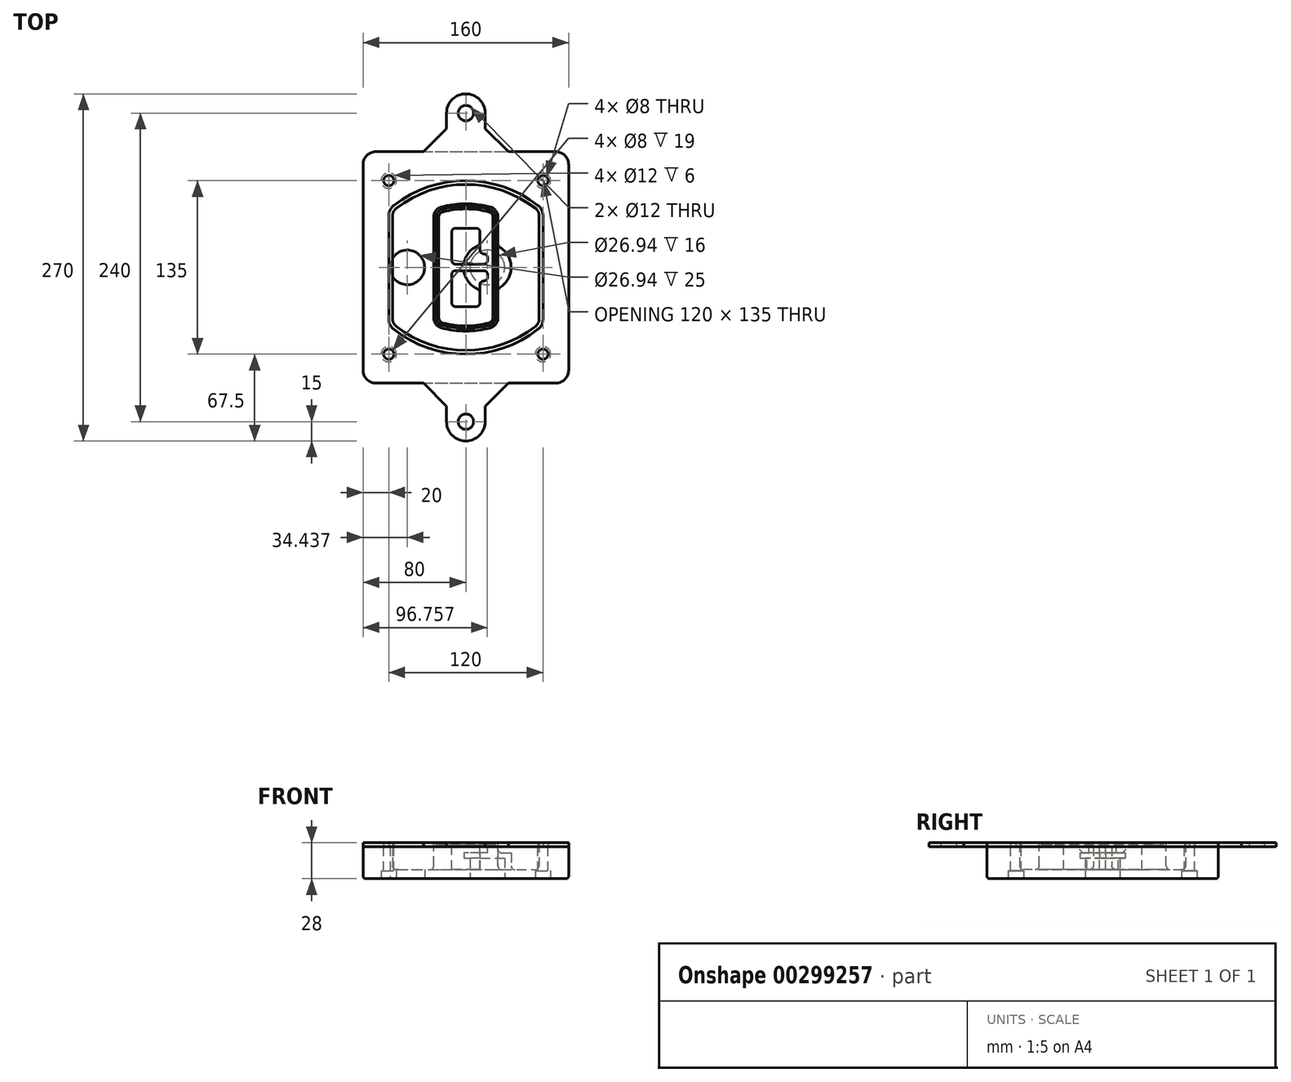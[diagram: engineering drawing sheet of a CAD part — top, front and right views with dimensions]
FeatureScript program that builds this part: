
annotation { "Feature Type Name" : "Feature", "Feature Type Description" : "" }
export const myFeature = defineFeature(function(context is Context, id is Id, definition is map)
    precondition{}
    {
        {
            var Q0;
            Q0=qCreatedBy(makeId("Top.planeOp"),FACE);
            var sketch = newSketch(context, id + "F0", { "sketchPlane" : qUnion([Q0])});
            skPoint(sketch, "E0.rect.middle", {"position": v(0, 0) * mm});
            skLineSegment(sketch, "E1.bottom", {"start": v(-70, -90) * mm, "end": v(70, -90) * mm});
            skLineSegment(sketch, "E1.top", {"start": v(-70, 90) * mm, "end": v(70, 90) * mm});
            skLineSegment(sketch, "E1.left", {"start": v(-80, -80) * mm, "end": v(-80, 80) * mm});
            skLineSegment(sketch, "E1.right", {"start": v(80, -80) * mm, "end": v(80, 80) * mm});
            skLineSegment(sketch, "E2", {"start": v(-80, 90) * mm, "end": v(80, -90) * mm, "construction": true});
            skLineSegment(sketch, "E3", {"start": v(80, 90) * mm, "end": v(-80, -90) * mm, "construction": true});
            skCircle(sketch, "E4", {"center": v(-60, 67.5) * mm, "radius": 4 * mm});
            skCircle(sketch, "E5", {"center": v(60, 67.5) * mm, "radius": 4 * mm});
            skCircle(sketch, "E6", {"center": v(60, -67.5) * mm, "radius": 4 * mm});
            skCircle(sketch, "E7", {"center": v(-60, -67.5) * mm, "radius": 4 * mm});
            skLineSegment(sketch, "E8", {"start": v(-60, 67.5) * mm, "end": v(60, 67.5) * mm, "construction": true});
            skLineSegment(sketch, "E9", {"start": v(60, 67.5) * mm, "end": v(60, -67.5) * mm, "construction": true});
            skLineSegment(sketch, "E10", {"start": v(60, -67.5) * mm, "end": v(-60, -67.5) * mm, "construction": true});
            skLineSegment(sketch, "E11", {"start": v(-60, -67.5) * mm, "end": v(-60, 67.5) * mm, "construction": true});
            skLineSegment(sketch, "E12", {"start": v(-60, 40.3) * mm, "end": v(-60, -40.3) * mm});
            skLineSegment(sketch, "E13", {"start": v(60, 40.3) * mm, "end": v(60, -40.3) * mm});
            skArc(sketch, "E14", {"start": v(56.15, 48.18) * mm, "mid": v(0, 67.5) * mm, "end": v(-56.15, 48.18) * mm});
            skArc(sketch, "E15", {"start": v(-56.15, -48.18) * mm, "mid": v(0, -67.5) * mm, "end": v(56.15, -48.18) * mm});
            skLineSegment(sketch, "E16", {"start": v(-60, 0) * mm, "end": v(60, 0) * mm, "construction": true});
            skPoint(sketch, "E17.visualSharp", {"position": v(-60, -45) * mm});
            skArc(sketch, "E17.filletArc", {"start": v(-60, -40.3) * mm, "mid": v(-58.99, -44.68) * mm, "end": v(-56.15, -48.18) * mm});
            skPoint(sketch, "E18.visualSharp", {"position": v(-60, 45) * mm});
            skArc(sketch, "E18.filletArc", {"start": v(-56.15, 48.18) * mm, "mid": v(-58.99, 44.68) * mm, "end": v(-60, 40.3) * mm});
            skPoint(sketch, "E19.visualSharp", {"position": v(60, 45) * mm});
            skArc(sketch, "E19.filletArc", {"start": v(60, 40.3) * mm, "mid": v(58.99, 44.68) * mm, "end": v(56.15, 48.18) * mm});
            skPoint(sketch, "E20.visualSharp", {"position": v(60, -45) * mm});
            skArc(sketch, "E20.filletArc", {"start": v(56.15, -48.18) * mm, "mid": v(58.99, -44.68) * mm, "end": v(60, -40.3) * mm});
            skPoint(sketch, "E21.visualSharp", {"position": v(-80, 90) * mm});
            skArc(sketch, "E21.filletArc", {"start": v(-70, 90) * mm, "mid": v(-77.07, 87.07) * mm, "end": v(-80, 80) * mm});
            skPoint(sketch, "E22.visualSharp", {"position": v(80, 90) * mm});
            skArc(sketch, "E22.filletArc", {"start": v(80, 80) * mm, "mid": v(77.07, 87.07) * mm, "end": v(70, 90) * mm});
            skPoint(sketch, "E23.visualSharp", {"position": v(80, -90) * mm});
            skArc(sketch, "E23.filletArc", {"start": v(70, -90) * mm, "mid": v(77.07, -87.07) * mm, "end": v(80, -80) * mm});
            skPoint(sketch, "E24.visualSharp", {"position": v(-80, -90) * mm});
            skArc(sketch, "E24.filletArc", {"start": v(-80, -80) * mm, "mid": v(-77.07, -87.07) * mm, "end": v(-70, -90) * mm});
            skArc(sketch, "E25.0", {"start": v(57, 40.3) * mm, "mid": v(56.3, 43.36) * mm, "end": v(54.3, 45.81) * mm});
            skLineSegment(sketch, "E25.1", {"start": v(57, 40.3) * mm, "end": v(57, -40.3) * mm});
            skArc(sketch, "E25.2", {"start": v(54.3, -45.81) * mm, "mid": v(56.3, -43.36) * mm, "end": v(57, -40.3) * mm});
            skArc(sketch, "E25.3", {"start": v(-54.3, -45.81) * mm, "mid": v(0, -64.5) * mm, "end": v(54.3, -45.81) * mm});
            skArc(sketch, "E25.4", {"start": v(-57, -40.3) * mm, "mid": v(-56.3, -43.36) * mm, "end": v(-54.3, -45.81) * mm});
            skArc(sketch, "E25.5", {"start": v(54.3, 45.81) * mm, "mid": v(0, 64.5) * mm, "end": v(-54.3, 45.81) * mm});
            skLineSegment(sketch, "E25.6", {"start": v(-57, 40.3) * mm, "end": v(-57, -40.3) * mm});
            skArc(sketch, "E25.7", {"start": v(-54.3, 45.81) * mm, "mid": v(-56.3, 43.36) * mm, "end": v(-57, 40.3) * mm});
            skArc(sketch, "E26.0", {"start": v(-58.62, 51.33) * mm, "mid": v(-62.58, 46.43) * mm, "end": v(-64, 40.3) * mm});
            skArc(sketch, "E26.1", {"start": v(58.62, 51.33) * mm, "mid": v(0, 71.5) * mm, "end": v(-58.62, 51.33) * mm});
            skArc(sketch, "E26.2", {"start": v(64, 40.3) * mm, "mid": v(62.58, 46.43) * mm, "end": v(58.62, 51.33) * mm});
            skLineSegment(sketch, "E26.3", {"start": v(64, 40.3) * mm, "end": v(64, -40.3) * mm});
            skArc(sketch, "E26.4", {"start": v(58.62, -51.33) * mm, "mid": v(62.58, -46.43) * mm, "end": v(64, -40.3) * mm});
            skLineSegment(sketch, "E26.5", {"start": v(-64, 40.3) * mm, "end": v(-64, -40.3) * mm});
            skArc(sketch, "E26.6", {"start": v(-58.62, -51.33) * mm, "mid": v(0, -71.5) * mm, "end": v(58.62, -51.33) * mm});
            skArc(sketch, "E26.7", {"start": v(-64, -40.3) * mm, "mid": v(-62.58, -46.43) * mm, "end": v(-58.62, -51.33) * mm});
            skSolve(sketch);
        }
        {
            var Q0;
            Q0=makeQuery(id+"F0.imprint","IMPRINT",FACE,{"disambiguationData":[TD([[makeQuery(id+"F0.imprint","IMPRINT",EDGE,{"derivedFrom":sQuery(id+"F0.wireOp",EDGE,"E1.bottom")}),1.0]])]});
            var Q1;
            Q1=makeQuery(id+"F0.imprint","IMPRINT",FACE,{"disambiguationData":[TD([[makeQuery(id+"F0.imprint","IMPRINT",EDGE,{"derivedFrom":sQuery(id+"F0.wireOp",EDGE,"E12")}),1.0]])]});
            var Q2;
            Q2=makeQuery(id+"F0.imprint","IMPRINT",FACE,{"disambiguationData":[TD([[makeQuery(id+"F0.imprint","IMPRINT",EDGE,{"derivedFrom":sQuery(id+"F0.wireOp",EDGE,"E25.0")}),1.0]])]});
            var Q3;
            Q3=makeQuery(id+"F0.imprint","IMPRINT",FACE,{"disambiguationData":[TD([[makeQuery(id+"F0.imprint","IMPRINT",EDGE,{"derivedFrom":sQuery(id+"F0.wireOp",EDGE,"E12")}),-1.0]])]});
            extrude(context, id + "F1", {"entities" : qUnion([Q0, Q1, Q2, Q3]), "oppositeDirection" : true, "depth" : 25 * mm});
        }
        {
            var Q0;
            Q0=makeQuery(id+"F0.imprint","IMPRINT",FACE,{"disambiguationData":[TD([[makeQuery(id+"F0.imprint","IMPRINT",EDGE,{"derivedFrom":sQuery(id+"F0.wireOp",EDGE,"E12")}),1.0]])]});
            extrude(context, id + "F2", {"entities" : qUnion([Q0]), "operationType" : NewBodyOperationType.ADD, "depth" : 3 * mm});
        }
        {
            var Q0;
            Q0=makeQuery(id+"F0.imprint","IMPRINT",FACE,{"disambiguationData":[TD([[makeQuery(id+"F0.imprint","IMPRINT",EDGE,{"derivedFrom":sQuery(id+"F0.wireOp",EDGE,"E25.0")}),1.0]])]});
            extrude(context, id + "F3", {"entities" : qUnion([Q0]), "operationType" : NewBodyOperationType.REMOVE, "oppositeDirection" : true, "depth" : 18 * mm});
        }
        {
            var Q0;
            Q0=makeQuery(id+"F2.opExtrude","CAP_FACE",FACE,{"disambiguationData":[OSD([sQuery(id+"F0.wireOp",EDGE,"E12"),sQuery(id+"F0.wireOp",EDGE,"E13"),sQuery(id+"F0.wireOp",EDGE,"E14"),sQuery(id+"F0.wireOp",EDGE,"E15"),sQuery(id+"F0.wireOp",EDGE,"E17.filletArc"),sQuery(id+"F0.wireOp",EDGE,"E18.filletArc"),sQuery(id+"F0.wireOp",EDGE,"E19.filletArc"),sQuery(id+"F0.wireOp",EDGE,"E20.filletArc"),sQuery(id+"F0.wireOp",EDGE,"E25.0"),sQuery(id+"F0.wireOp",EDGE,"E25.1"),sQuery(id+"F0.wireOp",EDGE,"E25.2"),sQuery(id+"F0.wireOp",EDGE,"E25.3"),sQuery(id+"F0.wireOp",EDGE,"E25.4"),sQuery(id+"F0.wireOp",EDGE,"E25.5"),sQuery(id+"F0.wireOp",EDGE,"E25.6"),sQuery(id+"F0.wireOp",EDGE,"E25.7")])],"isStart":false});
            var sketch = newSketch(context, id + "F4", { "sketchPlane" : qUnion([Q0])});
            skArc(sketch, "E27.0", {"start": v(-19.08, -46.97) * mm, "mid": v(0, -49.5) * mm, "end": v(19.08, -46.97) * mm});
            skArc(sketch, "E28.0", {"start": v(19.08, 46.97) * mm, "mid": v(0, 49.5) * mm, "end": v(-19.08, 46.97) * mm});
            skLineSegment(sketch, "E29", {"start": v(-25, 39.25) * mm, "end": v(-25, -39.25) * mm});
            skLineSegment(sketch, "E30", {"start": v(25, 39.25) * mm, "end": v(25, -39.25) * mm});
            skLineSegment(sketch, "E31", {"start": v(-25, 45.1) * mm, "end": v(25, 45.1) * mm, "construction": true});
            skLineSegment(sketch, "E32", {"start": v(-25, -45.1) * mm, "end": v(25, -45.1) * mm, "construction": true});
            skPoint(sketch, "E33.visualSharp", {"position": v(-25, 45.1) * mm});
            skArc(sketch, "E33.filletArc", {"start": v(-19.08, 46.97) * mm, "mid": v(-23.35, 44.11) * mm, "end": v(-25, 39.25) * mm});
            skPoint(sketch, "E34.visualSharp", {"position": v(25, 45.1) * mm});
            skArc(sketch, "E34.filletArc", {"start": v(25, 39.25) * mm, "mid": v(23.35, 44.11) * mm, "end": v(19.08, 46.97) * mm});
            skPoint(sketch, "E35.visualSharp", {"position": v(25, -45.1) * mm});
            skArc(sketch, "E35.filletArc", {"start": v(19.08, -46.97) * mm, "mid": v(23.35, -44.11) * mm, "end": v(25, -39.25) * mm});
            skPoint(sketch, "E36.visualSharp", {"position": v(-25, -45.1) * mm});
            skArc(sketch, "E36.filletArc", {"start": v(-25, -39.25) * mm, "mid": v(-23.35, -44.11) * mm, "end": v(-19.08, -46.97) * mm});
            skArc(sketch, "E37.0", {"start": v(54.3, 45.81) * mm, "mid": v(0, 64.5) * mm, "end": v(-54.3, 45.81) * mm});
            skArc(sketch, "E37.1", {"start": v(-54.3, 45.81) * mm, "mid": v(-56.3, 43.36) * mm, "end": v(-57, 40.3) * mm});
            skLineSegment(sketch, "E37.2", {"start": v(-57, 40.3) * mm, "end": v(-57, -40.3) * mm});
            skArc(sketch, "E37.3", {"start": v(-57, -40.3) * mm, "mid": v(-56.3, -43.36) * mm, "end": v(-54.3, -45.81) * mm});
            skArc(sketch, "E37.4", {"start": v(-54.3, -45.81) * mm, "mid": v(0, -64.5) * mm, "end": v(54.3, -45.81) * mm});
            skArc(sketch, "E37.5", {"start": v(54.3, -45.81) * mm, "mid": v(56.3, -43.36) * mm, "end": v(57, -40.3) * mm});
            skLineSegment(sketch, "E37.6", {"start": v(57, 40.3) * mm, "end": v(57, -40.3) * mm});
            skArc(sketch, "E37.7", {"start": v(57, 40.3) * mm, "mid": v(56.3, 43.36) * mm, "end": v(54.3, 45.81) * mm});
            skLineSegment(sketch, "E38.0", {"start": v(23, 39.25) * mm, "end": v(23, -39.25) * mm});
            skArc(sketch, "E38.1", {"start": v(18.56, -45.04) * mm, "mid": v(21.76, -42.9) * mm, "end": v(23, -39.25) * mm});
            skArc(sketch, "E38.2", {"start": v(-18.56, -45.04) * mm, "mid": v(0, -47.5) * mm, "end": v(18.56, -45.04) * mm});
            skArc(sketch, "E38.3", {"start": v(-23, -39.25) * mm, "mid": v(-21.76, -42.9) * mm, "end": v(-18.56, -45.04) * mm});
            skLineSegment(sketch, "E38.4", {"start": v(-23, 39.25) * mm, "end": v(-23, -39.25) * mm});
            skArc(sketch, "E38.5", {"start": v(23, 39.25) * mm, "mid": v(21.76, 42.9) * mm, "end": v(18.56, 45.04) * mm});
            skArc(sketch, "E38.6", {"start": v(-18.56, 45.04) * mm, "mid": v(-21.76, 42.9) * mm, "end": v(-23, 39.25) * mm});
            skArc(sketch, "E38.7", {"start": v(18.56, 45.04) * mm, "mid": v(0, 47.5) * mm, "end": v(-18.56, 45.04) * mm});
            skArc(sketch, "E39.0", {"start": v(21, 39.25) * mm, "mid": v(20.18, 41.68) * mm, "end": v(18.04, 43.1) * mm});
            skLineSegment(sketch, "E39.1", {"start": v(21, 39.25) * mm, "end": v(21, -39.25) * mm});
            skArc(sketch, "E39.2", {"start": v(18.04, -43.1) * mm, "mid": v(20.18, -41.68) * mm, "end": v(21, -39.25) * mm});
            skArc(sketch, "E39.3", {"start": v(-18.04, -43.1) * mm, "mid": v(0, -45.5) * mm, "end": v(18.04, -43.1) * mm});
            skArc(sketch, "E39.4", {"start": v(-21, -39.25) * mm, "mid": v(-20.18, -41.68) * mm, "end": v(-18.04, -43.1) * mm});
            skArc(sketch, "E39.5", {"start": v(18.04, 43.1) * mm, "mid": v(0, 45.5) * mm, "end": v(-18.04, 43.1) * mm});
            skLineSegment(sketch, "E39.6", {"start": v(-21, 39.25) * mm, "end": v(-21, -39.25) * mm});
            skArc(sketch, "E39.7", {"start": v(-18.04, 43.1) * mm, "mid": v(-20.18, 41.68) * mm, "end": v(-21, 39.25) * mm});
            skLineSegment(sketch, "E40", {"start": v(-25, 0) * mm, "end": v(25, 0) * mm, "construction": true});
            skLineSegment(sketch, "E41", {"start": v(-11, 5.5) * mm, "end": v(-11, 27.5) * mm});
            skLineSegment(sketch, "E42", {"start": v(-8, 30.5) * mm, "end": v(8, 30.5) * mm});
            skLineSegment(sketch, "E43", {"start": v(11, 27.5) * mm, "end": v(11, 13.5) * mm});
            skLineSegment(sketch, "E44", {"start": v(14, 10.5) * mm, "end": v(14, 10.5) * mm});
            skLineSegment(sketch, "E45", {"start": v(17, 7.5) * mm, "end": v(17, 5.5) * mm});
            skLineSegment(sketch, "E46", {"start": v(14, 2.5) * mm, "end": v(-8, 2.5) * mm});
            skPoint(sketch, "E47.visualSharp", {"position": v(-11, 30.5) * mm});
            skArc(sketch, "E47.filletArc", {"start": v(-8, 30.5) * mm, "mid": v(-10.12, 29.62) * mm, "end": v(-11, 27.5) * mm});
            skPoint(sketch, "E48.visualSharp", {"position": v(11, 30.5) * mm});
            skArc(sketch, "E48.filletArc", {"start": v(11, 27.5) * mm, "mid": v(10.12, 29.62) * mm, "end": v(8, 30.5) * mm});
            skPoint(sketch, "E49.visualSharp", {"position": v(11, 10.5) * mm});
            skArc(sketch, "E49.filletArc", {"start": v(11, 13.5) * mm, "mid": v(11.88, 11.38) * mm, "end": v(14, 10.5) * mm});
            skPoint(sketch, "E50.visualSharp", {"position": v(17, 10.5) * mm});
            skArc(sketch, "E50.filletArc", {"start": v(17, 7.5) * mm, "mid": v(16.12, 9.62) * mm, "end": v(14, 10.5) * mm});
            skPoint(sketch, "E51.visualSharp", {"position": v(17, 2.5) * mm});
            skArc(sketch, "E51.filletArc", {"start": v(14, 2.5) * mm, "mid": v(16.12, 3.38) * mm, "end": v(17, 5.5) * mm});
            skPoint(sketch, "E52.visualSharp", {"position": v(-11, 2.5) * mm});
            skArc(sketch, "E52.filletArc", {"start": v(-11, 5.5) * mm, "mid": v(-10.12, 3.38) * mm, "end": v(-8, 2.5) * mm});
            skLineSegment(sketch, "E53.0.MirrorCS", {"start": v(14, -2.5) * mm, "end": v(-8, -2.5) * mm});
            skArc(sketch, "E54.0.MirrorCS", {"start": v(-11, -5.5) * mm, "mid": v(-10.12, -3.38) * mm, "end": v(-8, -2.5) * mm});
            skLineSegment(sketch, "E55.0.MirrorCS", {"start": v(-11, -5.5) * mm, "end": v(-11, -27.5) * mm});
            skArc(sketch, "E56.0.MirrorCS", {"start": v(-8, -30.5) * mm, "mid": v(-10.12, -29.62) * mm, "end": v(-11, -27.5) * mm});
            skLineSegment(sketch, "E57.0.MirrorCS", {"start": v(-8, -30.5) * mm, "end": v(8, -30.5) * mm});
            skArc(sketch, "E58.0.MirrorCS", {"start": v(11, -27.5) * mm, "mid": v(10.12, -29.62) * mm, "end": v(8, -30.5) * mm});
            skLineSegment(sketch, "E59.0.MirrorCS", {"start": v(11, -27.5) * mm, "end": v(11, -13.5) * mm});
            skArc(sketch, "E60.0.MirrorCS", {"start": v(11, -13.5) * mm, "mid": v(11.88, -11.38) * mm, "end": v(14, -10.5) * mm});
            skArc(sketch, "E61.0.MirrorCS", {"start": v(17, -7.5) * mm, "mid": v(16.12, -9.62) * mm, "end": v(14, -10.5) * mm});
            skLineSegment(sketch, "E62.0.MirrorCS", {"start": v(17, -7.5) * mm, "end": v(17, -5.5) * mm});
            skArc(sketch, "E63.0.MirrorCS", {"start": v(14, -2.5) * mm, "mid": v(16.12, -3.38) * mm, "end": v(17, -5.5) * mm});
            skSolve(sketch);
        }
        {
            var Q0;
            Q0=makeQuery(id+"F4.imprint","IMPRINT",FACE,{"disambiguationData":[TD([[makeQuery(id+"F4.imprint","IMPRINT",EDGE,{"derivedFrom":sQuery(id+"F4.wireOp",EDGE,"E27.0")}),1.0]])]});
            var Q1;
            Q1=makeQuery(id+"F4.imprint","IMPRINT",FACE,{"disambiguationData":[TD([[makeQuery(id+"F4.imprint","IMPRINT",EDGE,{"derivedFrom":sQuery(id+"F4.wireOp",EDGE,"E38.0")}),-1.0]])]});
            var Q2;
            Q2=makeQuery(id+"F4.imprint","IMPRINT",FACE,{"disambiguationData":[TD([[makeQuery(id+"F4.imprint","IMPRINT",EDGE,{"derivedFrom":sQuery(id+"F4.wireOp",EDGE,"E39.0")}),1.0]])]});
            extrude(context, id + "F5", {"entities" : qUnion([Q0, Q1, Q2]), "operationType" : NewBodyOperationType.ADD, "endBound" : BoundingType.UP_TO_NEXT, "oppositeDirection" : true, "depth" : 25 * mm});
        }
        {
            var Q0;
            Q0=makeQuery(id+"F4.imprint","IMPRINT",FACE,{"disambiguationData":[TD([[makeQuery(id+"F4.imprint","IMPRINT",EDGE,{"derivedFrom":sQuery(id+"F4.wireOp",EDGE,"E38.0")}),-1.0]])]});
            extrude(context, id + "F6", {"entities" : qUnion([Q0]), "operationType" : NewBodyOperationType.REMOVE, "oppositeDirection" : true, "depth" : 2 * mm});
        }
        {
            var Q0;
            Q0=makeQuery(id+"F1.opExtrude","CAP_FACE",FACE,{"disambiguationData":[OSD([sQuery(id+"F0.wireOp",EDGE,"E1.bottom"),sQuery(id+"F0.wireOp",EDGE,"E1.top"),sQuery(id+"F0.wireOp",EDGE,"E1.left"),sQuery(id+"F0.wireOp",EDGE,"E1.right"),sQuery(id+"F0.wireOp",EDGE,"E4"),sQuery(id+"F0.wireOp",EDGE,"E5"),sQuery(id+"F0.wireOp",EDGE,"E6"),sQuery(id+"F0.wireOp",EDGE,"E7"),sQuery(id+"F0.wireOp",EDGE,"E21.filletArc"),sQuery(id+"F0.wireOp",EDGE,"E22.filletArc"),sQuery(id+"F0.wireOp",EDGE,"E23.filletArc"),sQuery(id+"F0.wireOp",EDGE,"E24.filletArc")])],"isStart":false});
            var sketch = newSketch(context, id + "F7", { "sketchPlane" : qUnion([Q0])});
            skCircle(sketch, "E64", {"center": v(16.76, 0) * mm, "radius": 13.47 * mm});
            skCircle(sketch, "E65", {"center": v(-45.56, 0) * mm, "radius": 13.47 * mm});
            skLineSegment(sketch, "E66", {"start": v(80, 0) * mm, "end": v(-80, 0) * mm});
            skCircle(sketch, "E67", {"center": v(16.76, 0) * mm, "radius": 18.47 * mm});
            skCircle(sketch, "E68", {"center": v(60, -67.5) * mm, "radius": 6 * mm});
            skCircle(sketch, "E69", {"center": v(-60, -67.5) * mm, "radius": 6 * mm});
            skCircle(sketch, "E70", {"center": v(-60, 67.5) * mm, "radius": 6 * mm});
            skCircle(sketch, "E71", {"center": v(60, 67.5) * mm, "radius": 6 * mm});
            skSolve(sketch);
        }
        {
            var Q0;
            {var subQ1=sQuery(id+"F7.wireOp",EDGE,"E66");var subQ4=sQuery(id+"F7.wireOp",EDGE,"E64");var subQ6=makeQuery(id+"F7.imprint","INTERSECT",VERTEX,{"disambiguationData":[OD(0.0)],"derivedFrom":[subQ4,subQ1]});Q0=makeQuery(id+"F7.imprint","IMPRINT",FACE,{"disambiguationData":[TD([[makeQuery(id+"F7.imprint","IMPRINT",EDGE,{"disambiguationData":[TD([[subQ6,-1.0]])],"derivedFrom":subQ4}),-1.0]])]});}
            var Q1;
            {var subQ0=sQuery(id+"F7.wireOp",EDGE,"E66");var subQ1=sQuery(id+"F7.wireOp",EDGE,"E64");var subQ3=makeQuery(id+"F7.imprint","INTERSECT",VERTEX,{"disambiguationData":[OD(0.0)],"derivedFrom":[subQ1,subQ0]});Q1=makeQuery(id+"F7.imprint","IMPRINT",FACE,{"disambiguationData":[TD([[makeQuery(id+"F7.imprint","IMPRINT",EDGE,{"disambiguationData":[TD([[subQ3,-1.0]])],"derivedFrom":subQ1}),1.0]])]});}
            var Q2;
            {var subQ0=sQuery(id+"F7.wireOp",EDGE,"E66");var subQ1=sQuery(id+"F7.wireOp",EDGE,"E64");var subQ3=makeQuery(id+"F7.imprint","INTERSECT",VERTEX,{"disambiguationData":[OD(0.0)],"derivedFrom":[subQ1,subQ0]});Q2=makeQuery(id+"F7.imprint","IMPRINT",FACE,{"disambiguationData":[TD([[makeQuery(id+"F7.imprint","IMPRINT",EDGE,{"disambiguationData":[TD([[subQ3,1.0]])],"derivedFrom":subQ1}),1.0]])]});}
            var Q3;
            {var subQ1=sQuery(id+"F7.wireOp",EDGE,"E66");var subQ4=sQuery(id+"F7.wireOp",EDGE,"E64");var subQ6=makeQuery(id+"F7.imprint","INTERSECT",VERTEX,{"disambiguationData":[OD(0.0)],"derivedFrom":[subQ4,subQ1]});Q3=makeQuery(id+"F7.imprint","IMPRINT",FACE,{"disambiguationData":[TD([[makeQuery(id+"F7.imprint","IMPRINT",EDGE,{"disambiguationData":[TD([[subQ6,1.0]])],"derivedFrom":subQ4}),-1.0]])]});}
            extrude(context, id + "F8", {"entities" : qUnion([Q0, Q1, Q2, Q3]), "operationType" : NewBodyOperationType.ADD, "oppositeDirection" : true, "depth" : 20 * mm});
        }
        {
            var Q0;
            {var subQ0=sQuery(id+"F7.wireOp",EDGE,"E66");var subQ1=sQuery(id+"F7.wireOp",EDGE,"E64");var subQ3=makeQuery(id+"F7.imprint","INTERSECT",VERTEX,{"disambiguationData":[OD(0.0)],"derivedFrom":[subQ1,subQ0]});Q0=makeQuery(id+"F7.imprint","IMPRINT",FACE,{"disambiguationData":[TD([[makeQuery(id+"F7.imprint","IMPRINT",EDGE,{"disambiguationData":[TD([[subQ3,-1.0]])],"derivedFrom":subQ1}),1.0]])]});}
            var Q1;
            {var subQ0=sQuery(id+"F7.wireOp",EDGE,"E66");var subQ1=sQuery(id+"F7.wireOp",EDGE,"E64");var subQ3=makeQuery(id+"F7.imprint","INTERSECT",VERTEX,{"disambiguationData":[OD(0.0)],"derivedFrom":[subQ1,subQ0]});Q1=makeQuery(id+"F7.imprint","IMPRINT",FACE,{"disambiguationData":[TD([[makeQuery(id+"F7.imprint","IMPRINT",EDGE,{"disambiguationData":[TD([[subQ3,1.0]])],"derivedFrom":subQ1}),1.0]])]});}
            extrude(context, id + "F9", {"entities" : qUnion([Q0, Q1]), "operationType" : NewBodyOperationType.REMOVE, "oppositeDirection" : true, "depth" : 16 * mm});
        }
        {
            var Q0;
            {var subQ0=sQuery(id+"F7.wireOp",EDGE,"E66");var subQ1=sQuery(id+"F7.wireOp",EDGE,"E65");var subQ3=makeQuery(id+"F7.imprint","INTERSECT",VERTEX,{"disambiguationData":[OD(0.0)],"derivedFrom":[subQ1,subQ0]});Q0=makeQuery(id+"F7.imprint","IMPRINT",FACE,{"disambiguationData":[TD([[makeQuery(id+"F7.imprint","IMPRINT",EDGE,{"disambiguationData":[TD([[subQ3,-1.0]])],"derivedFrom":subQ1}),1.0]])]});}
            var Q1;
            {var subQ0=sQuery(id+"F7.wireOp",EDGE,"E66");var subQ1=sQuery(id+"F7.wireOp",EDGE,"E65");var subQ3=makeQuery(id+"F7.imprint","INTERSECT",VERTEX,{"disambiguationData":[OD(0.0)],"derivedFrom":[subQ1,subQ0]});Q1=makeQuery(id+"F7.imprint","IMPRINT",FACE,{"disambiguationData":[TD([[makeQuery(id+"F7.imprint","IMPRINT",EDGE,{"disambiguationData":[TD([[subQ3,1.0]])],"derivedFrom":subQ1}),1.0]])]});}
            extrude(context, id + "F10", {"entities" : qUnion([Q0, Q1]), "operationType" : NewBodyOperationType.REMOVE, "oppositeDirection" : true, "depth" : 25 * mm});
        }
        {
            var Q0;
            Q0=makeQuery(id+"F7.imprint","IMPRINT",FACE,{"disambiguationData":[TD([[makeQuery(id+"F7.imprint","IMPRINT",EDGE,{"derivedFrom":sQuery(id+"F7.wireOp",EDGE,"E68")}),1.0]])]});
            var Q1;
            Q1=makeQuery(id+"F7.imprint","IMPRINT",FACE,{"disambiguationData":[TD([[makeQuery(id+"F7.imprint","IMPRINT",EDGE,{"derivedFrom":makeQuery(id+"F1.opExtrude","CAP_EDGE",EDGE,{"disambiguationData":[OSD([sQuery(id+"F0.wireOp",EDGE,"E5")])],"isStart":false})}),-1.0]])]});
            var Q2;
            Q2=makeQuery(id+"F7.imprint","IMPRINT",FACE,{"disambiguationData":[TD([[makeQuery(id+"F7.imprint","IMPRINT",EDGE,{"derivedFrom":sQuery(id+"F7.wireOp",EDGE,"E69")}),1.0]])]});
            var Q3;
            Q3=makeQuery(id+"F7.imprint","IMPRINT",FACE,{"disambiguationData":[TD([[makeQuery(id+"F7.imprint","IMPRINT",EDGE,{"derivedFrom":makeQuery(id+"F1.opExtrude","CAP_EDGE",EDGE,{"disambiguationData":[OSD([sQuery(id+"F0.wireOp",EDGE,"E4")])],"isStart":false})}),-1.0]])]});
            var Q4;
            Q4=makeQuery(id+"F7.imprint","IMPRINT",FACE,{"disambiguationData":[TD([[makeQuery(id+"F7.imprint","IMPRINT",EDGE,{"derivedFrom":sQuery(id+"F7.wireOp",EDGE,"E70")}),1.0]])]});
            var Q5;
            Q5=makeQuery(id+"F7.imprint","IMPRINT",FACE,{"disambiguationData":[TD([[makeQuery(id+"F7.imprint","IMPRINT",EDGE,{"derivedFrom":makeQuery(id+"F1.opExtrude","CAP_EDGE",EDGE,{"disambiguationData":[OSD([sQuery(id+"F0.wireOp",EDGE,"E7")])],"isStart":false})}),-1.0]])]});
            var Q6;
            Q6=makeQuery(id+"F7.imprint","IMPRINT",FACE,{"disambiguationData":[TD([[makeQuery(id+"F7.imprint","IMPRINT",EDGE,{"derivedFrom":sQuery(id+"F7.wireOp",EDGE,"E71")}),1.0]])]});
            var Q7;
            Q7=makeQuery(id+"F7.imprint","IMPRINT",FACE,{"disambiguationData":[TD([[makeQuery(id+"F7.imprint","IMPRINT",EDGE,{"derivedFrom":makeQuery(id+"F1.opExtrude","CAP_EDGE",EDGE,{"disambiguationData":[OSD([sQuery(id+"F0.wireOp",EDGE,"E6")])],"isStart":false})}),-1.0]])]});
            extrude(context, id + "F11", {"entities" : qUnion([Q0, Q1, Q2, Q3, Q4, Q5, Q6, Q7]), "operationType" : NewBodyOperationType.REMOVE, "oppositeDirection" : true, "depth" : 6 * mm});
        }
        {
            var Q0;
            Q0=makeQuery(id+"F9.boolean.opBoolean","COPY",FACE,{"derivedFrom":makeQuery(id+"F9.opExtrude","CAP_FACE",FACE,{"disambiguationData":[OSD([sQuery(id+"F7.wireOp",EDGE,"E64")])],"isStart":false})});
            var sketch = newSketch(context, id + "F12", { "sketchPlane" : qUnion([Q0])});
            skArc(sketch, "E72.0", {"start": v(11, 17.55) * mm, "mid": v(2.57, 11.82) * mm, "end": v(-1.54, 2.5) * mm});
            skArc(sketch, "E72.1", {"start": v(-1.54, -2.5) * mm, "mid": v(2.57, -11.82) * mm, "end": v(11, -17.55) * mm});
            skLineSegment(sketch, "E73", {"start": v(-1.54, -2.5) * mm, "end": v(14, -2.5) * mm});
            skLineSegment(sketch, "E74.0", {"start": v(14, 2.5) * mm, "end": v(-1.54, 2.5) * mm});
            skArc(sketch, "E74.1", {"start": v(14, 2.5) * mm, "mid": v(16.12, 3.38) * mm, "end": v(17, 5.5) * mm});
            skLineSegment(sketch, "E74.2", {"start": v(17, 7.5) * mm, "end": v(17, 5.5) * mm});
            skArc(sketch, "E74.3", {"start": v(17, 7.5) * mm, "mid": v(16.12, 9.62) * mm, "end": v(14, 10.5) * mm});
            skArc(sketch, "E74.4", {"start": v(11, 13.5) * mm, "mid": v(11.88, 11.38) * mm, "end": v(14, 10.5) * mm});
            skLineSegment(sketch, "E74.5", {"start": v(11, 17.55) * mm, "end": v(11, 13.5) * mm});
            skLineSegment(sketch, "E74.7", {"start": v(14, -2.5) * mm, "end": v(-1.54, -2.5) * mm});
            skArc(sketch, "E74.8", {"start": v(14, -2.5) * mm, "mid": v(16.12, -3.38) * mm, "end": v(17, -5.5) * mm});
            skLineSegment(sketch, "E74.9", {"start": v(17, -7.5) * mm, "end": v(17, -5.5) * mm});
            skArc(sketch, "E74.10", {"start": v(17, -7.5) * mm, "mid": v(16.12, -9.62) * mm, "end": v(14, -10.5) * mm});
            skArc(sketch, "E74.11", {"start": v(11, -13.5) * mm, "mid": v(11.88, -11.38) * mm, "end": v(14, -10.5) * mm});
            skLineSegment(sketch, "E74.12", {"start": v(11, -17.55) * mm, "end": v(11, -13.5) * mm});
            skPoint(sketch, "E75.orphan", {"position": v(11, -27.5) * mm});
            skPoint(sketch, "E76.orphan", {"position": v(-8, -2.5) * mm});
            skPoint(sketch, "E77.orphan", {"position": v(-8, 2.5) * mm});
            skPoint(sketch, "E78.orphan", {"position": v(11, 27.5) * mm});
            skSolve(sketch);
        }
        {
            var Q0;
            {var subQ7=sQuery(id+"F12.wireOp",EDGE,"E72.0");var subQ14=sQuery(id+"F12.wireOp",EDGE,"E72.1");var subQ16=sQuery(id+"F12.wireOp",EDGE,"E74.1");var subQ18=sQuery(id+"F12.wireOp",EDGE,"E74.8");Q0=qUnion([makeQuery(id+"F12.imprint","IMPRINT",FACE,{"disambiguationData":[TD([[makeQuery(id+"F12.imprint","IMPRINT",EDGE,{"derivedFrom":subQ7}),1.0]])]}),makeQuery(id+"F12.imprint","IMPRINT",FACE,{"disambiguationData":[TD([[makeQuery(id+"F12.imprint","IMPRINT",EDGE,{"derivedFrom":subQ14}),1.0]])]}),makeQuery(id+"F12.imprint","IMPRINT",FACE,{"disambiguationData":[TD([[makeQuery(id+"F12.imprint","IMPRINT",EDGE,{"derivedFrom":subQ16}),1.0]])]}),makeQuery(id+"F12.imprint","IMPRINT",FACE,{"disambiguationData":[TD([[makeQuery(id+"F12.imprint","IMPRINT",EDGE,{"derivedFrom":subQ18}),-1.0]])]})]);}
            var Q1;
            Q1=makeQuery(id+"F5.boolean.opBoolean","SPLIT",FACE,{"disambiguationData":[TD([makeQuery(id+"F5.opExtrude","SWEPT_FACE",FACE,{"disambiguationData":[OSD([sQuery(id+"F4.wireOp",EDGE,"E41")])]})])],"derivedFrom":makeQuery(id+"F3.boolean.opBoolean","COPY",FACE,{"derivedFrom":makeQuery(id+"F3.opExtrude","CAP_FACE",FACE,{"disambiguationData":[OSD([sQuery(id+"F0.wireOp",EDGE,"E25.0"),sQuery(id+"F0.wireOp",EDGE,"E25.1"),sQuery(id+"F0.wireOp",EDGE,"E25.2"),sQuery(id+"F0.wireOp",EDGE,"E25.3"),sQuery(id+"F0.wireOp",EDGE,"E25.4"),sQuery(id+"F0.wireOp",EDGE,"E25.5"),sQuery(id+"F0.wireOp",EDGE,"E25.6"),sQuery(id+"F0.wireOp",EDGE,"E25.7")])],"isStart":false})})});
            extrude(context, id + "F13", {"entities" : qUnion([Q0]), "operationType" : NewBodyOperationType.REMOVE, "endBound" : BoundingType.UP_TO_SURFACE, "endBoundEntityFace" : qUnion([Q1]), "depth" : 25 * mm});
        }
        {
            var Q0;
            Q0=makeQuery(id+"F3.boolean.opBoolean","COPY",EDGE,{"derivedFrom":makeQuery(id+"F3.opExtrude","CAP_EDGE",EDGE,{"disambiguationData":[OSD([sQuery(id+"F0.wireOp",EDGE,"E25.6")])],"isStart":false})});
            var Q1;
            Q1=makeQuery(id+"F8.boolean.opBoolean","INTERSECT",EDGE,{"derivedFrom":[makeQuery(id+"F5.opExtrude","SWEPT_FACE",FACE,{"disambiguationData":[OSD([sQuery(id+"F4.wireOp",EDGE,"E30")])]}),makeQuery(id+"F8.opExtrude","CAP_FACE",FACE,{"disambiguationData":[OSD([sQuery(id+"F7.wireOp",EDGE,"E67")])],"isStart":false})]});
            var Q2;
            Q2=makeQuery(id+"F8.boolean.opBoolean","INTERSECT",EDGE,{"disambiguationData":[OD(1.0)],"derivedFrom":[makeQuery(id+"F5.opExtrude","SWEPT_FACE",FACE,{"disambiguationData":[OSD([sQuery(id+"F4.wireOp",EDGE,"E30")])]}),makeQuery(id+"F8.opExtrude","SWEPT_FACE",FACE,{"disambiguationData":[OSD([sQuery(id+"F7.wireOp",EDGE,"E67")])]})]});
            var Q3;
            {var subQ0=sQuery(id+"F4.wireOp",EDGE,"E30");Q3=makeQuery(id+"F8.boolean.opBoolean","SPLIT",EDGE,{"disambiguationData":[TD([makeQuery(id+"F5.opExtrude","SWEPT_FACE",FACE,{"disambiguationData":[OSD([sQuery(id+"F4.wireOp",EDGE,"E35.filletArc")])]})])],"derivedFrom":makeQuery(id+"F5.opExtrude","CAP_EDGE",EDGE,{"disambiguationData":[OSD([subQ0])],"isStart":false})});}
            var Q4;
            {var subQ0=sQuery(id+"F0.wireOp",EDGE,"E25.7");var subQ1=sQuery(id+"F0.wireOp",EDGE,"E25.1");var subQ2=sQuery(id+"F0.wireOp",EDGE,"E25.6");var subQ3=sQuery(id+"F0.wireOp",EDGE,"E25.5");var subQ4=sQuery(id+"F0.wireOp",EDGE,"E25.4");var subQ5=sQuery(id+"F0.wireOp",EDGE,"E25.0");var subQ6=sQuery(id+"F0.wireOp",EDGE,"E25.2");var subQ7=sQuery(id+"F0.wireOp",EDGE,"E25.3");Q4=makeQuery(id+"F8.boolean.opBoolean","INTERSECT",EDGE,{"derivedFrom":[makeQuery(id+"F5.boolean.opBoolean","SPLIT",FACE,{"disambiguationData":[TD([makeQuery(id+"F2.opExtrude","SWEPT_FACE",FACE,{"disambiguationData":[OSD([subQ5])]})])],"derivedFrom":makeQuery(id+"F3.boolean.opBoolean","COPY",FACE,{"derivedFrom":makeQuery(id+"F3.opExtrude","CAP_FACE",FACE,{"disambiguationData":[OSD([subQ5,subQ1,subQ6,subQ7,subQ4,subQ3,subQ2,subQ0])],"isStart":false})})}),makeQuery(id+"F8.opExtrude","SWEPT_FACE",FACE,{"disambiguationData":[OSD([sQuery(id+"F7.wireOp",EDGE,"E67")])]})]});}
            var Q5;
            Q5=makeQuery(id+"F8.boolean.opBoolean","INTERSECT",EDGE,{"disambiguationData":[OD(0.0)],"derivedFrom":[makeQuery(id+"F5.opExtrude","SWEPT_FACE",FACE,{"disambiguationData":[OSD([sQuery(id+"F4.wireOp",EDGE,"E30")])]}),makeQuery(id+"F8.opExtrude","SWEPT_FACE",FACE,{"disambiguationData":[OSD([sQuery(id+"F7.wireOp",EDGE,"E67")])]})]});
            fillet(context, id + "F14", {"entities" : qUnion([Q0, Q1, Q2, Q3, Q4, Q5]), "radius" : 3 * mm, "tangentPropagation" : true, "allowEdgeOverflow" : false});
        }
        {
            var Q0;
            Q0=makeQuery(id+"F1.opExtrude","CAP_EDGE",EDGE,{"disambiguationData":[OSD([sQuery(id+"F0.wireOp",EDGE,"E1.bottom")])],"isStart":false});
            fillet(context, id + "F15", {"entities" : qUnion([Q0]), "radius" : 2 * mm, "tangentPropagation" : true, "allowEdgeOverflow" : false});
        }
        {
            var Q0;
            {var subQ0=sQuery(id+"F0.wireOp",EDGE,"E21.filletArc");var subQ1=sQuery(id+"F0.wireOp",EDGE,"E7");var subQ2=sQuery(id+"F0.wireOp",EDGE,"E6");var subQ3=sQuery(id+"F0.wireOp",EDGE,"E5");var subQ4=sQuery(id+"F0.wireOp",EDGE,"E4");var subQ5=sQuery(id+"F0.wireOp",EDGE,"E22.filletArc");var subQ6=sQuery(id+"F0.wireOp",EDGE,"E1.bottom");var subQ7=sQuery(id+"F0.wireOp",EDGE,"E1.right");var subQ8=sQuery(id+"F0.wireOp",EDGE,"E1.top");var subQ9=sQuery(id+"F0.wireOp",EDGE,"E1.left");var subQ10=sQuery(id+"F0.wireOp",EDGE,"E23.filletArc");var subQ11=sQuery(id+"F0.wireOp",EDGE,"E24.filletArc");Q0=makeQuery(id+"F2.boolean.opBoolean","SPLIT",FACE,{"disambiguationData":[TD([makeQuery(id+"F1.opExtrude","SWEPT_FACE",FACE,{"disambiguationData":[OSD([subQ6])]})])],"derivedFrom":makeQuery(id+"F1.opExtrude","CAP_FACE",FACE,{"disambiguationData":[OSD([subQ6,subQ8,subQ9,subQ7,subQ4,subQ3,subQ2,subQ1,subQ0,subQ5,subQ10,subQ11])],"isStart":true})});}
            var sketch = newSketch(context, id + "F16", { "sketchPlane" : qUnion([Q0])});
            skLineSegment(sketch, "E79", {"start": v(0, 90) * mm, "end": v(0, 120) * mm});
            skCircle(sketch, "E80", {"center": v(0, 120) * mm, "radius": 6 * mm});
            skArc(sketch, "E81", {"start": v(15, 120) * mm, "mid": v(0, 135) * mm, "end": v(-15, 120) * mm});
            skLineSegment(sketch, "E82", {"start": v(-15, 120) * mm, "end": v(-15, 108) * mm});
            skLineSegment(sketch, "E83", {"start": v(-15, 108) * mm, "end": v(-33, 90) * mm});
            skLineSegment(sketch, "E84", {"start": v(15, 120) * mm, "end": v(15, 108) * mm});
            skLineSegment(sketch, "E85", {"start": v(15, 108) * mm, "end": v(33, 90) * mm});
            skLineSegment(sketch, "E86", {"start": v(-80, 0) * mm, "end": v(80, 0) * mm, "construction": true});
            skLineSegment(sketch, "E87.MirrorCS", {"start": v(15, -120) * mm, "end": v(15, -108) * mm});
            skLineSegment(sketch, "E88.MirrorCS", {"start": v(-15, -120) * mm, "end": v(-15, -108) * mm});
            skLineSegment(sketch, "E89.MirrorCS", {"start": v(15, -108) * mm, "end": v(33, -90) * mm});
            skCircle(sketch, "E90.MirrorC", {"center": v(0, -120) * mm, "radius": 6 * mm});
            skLineSegment(sketch, "E91.MirrorCS", {"start": v(0, -90) * mm, "end": v(0, -120) * mm});
            skArc(sketch, "E92.MirrorCS", {"start": v(15, -120) * mm, "mid": v(0, -135) * mm, "end": v(-15, -120) * mm});
            skLineSegment(sketch, "E93.MirrorCS", {"start": v(-15, -108) * mm, "end": v(-33, -90) * mm});
            skSolve(sketch);
        }
        {
            var Q0;
            Q0=makeQuery(id+"F16.imprint","IMPRINT",FACE,{"disambiguationData":[TD([[makeQuery(id+"F16.imprint","IMPRINT",EDGE,{"derivedFrom":makeQuery(id+"F1.opExtrude","CAP_EDGE",EDGE,{"disambiguationData":[OSD([sQuery(id+"F0.wireOp",EDGE,"E1.left")])],"isStart":true})}),-1.0]])]});
            var Q1;
            Q1=makeQuery(id+"F16.imprint","IMPRINT",FACE,{"disambiguationData":[TD([[makeQuery(id+"F16.imprint","IMPRINT",EDGE,{"derivedFrom":sQuery(id+"F16.wireOp",EDGE,"E80")}),-1.0]])]});
            var Q2;
            Q2=makeQuery(id+"F16.imprint","IMPRINT",FACE,{"disambiguationData":[TD([[makeQuery(id+"F16.imprint","IMPRINT",EDGE,{"derivedFrom":sQuery(id+"F16.wireOp",EDGE,"E87.MirrorCS")}),1.0]])]});
            var Q3;
            Q3=makeQuery(id+"F2.opExtrude","CAP_FACE",FACE,{"disambiguationData":[OSD([sQuery(id+"F0.wireOp",EDGE,"E12"),sQuery(id+"F0.wireOp",EDGE,"E13"),sQuery(id+"F0.wireOp",EDGE,"E14"),sQuery(id+"F0.wireOp",EDGE,"E15"),sQuery(id+"F0.wireOp",EDGE,"E17.filletArc"),sQuery(id+"F0.wireOp",EDGE,"E18.filletArc"),sQuery(id+"F0.wireOp",EDGE,"E19.filletArc"),sQuery(id+"F0.wireOp",EDGE,"E20.filletArc"),sQuery(id+"F0.wireOp",EDGE,"E25.0"),sQuery(id+"F0.wireOp",EDGE,"E25.1"),sQuery(id+"F0.wireOp",EDGE,"E25.2"),sQuery(id+"F0.wireOp",EDGE,"E25.3"),sQuery(id+"F0.wireOp",EDGE,"E25.4"),sQuery(id+"F0.wireOp",EDGE,"E25.5"),sQuery(id+"F0.wireOp",EDGE,"E25.6"),sQuery(id+"F0.wireOp",EDGE,"E25.7")])],"isStart":false});
            extrude(context, id + "F17", {"entities" : qUnion([Q0, Q1, Q2]), "endBound" : BoundingType.UP_TO_SURFACE, "endBoundEntityFace" : qUnion([Q3]), "depth" : 25 * mm});
        }
    });
